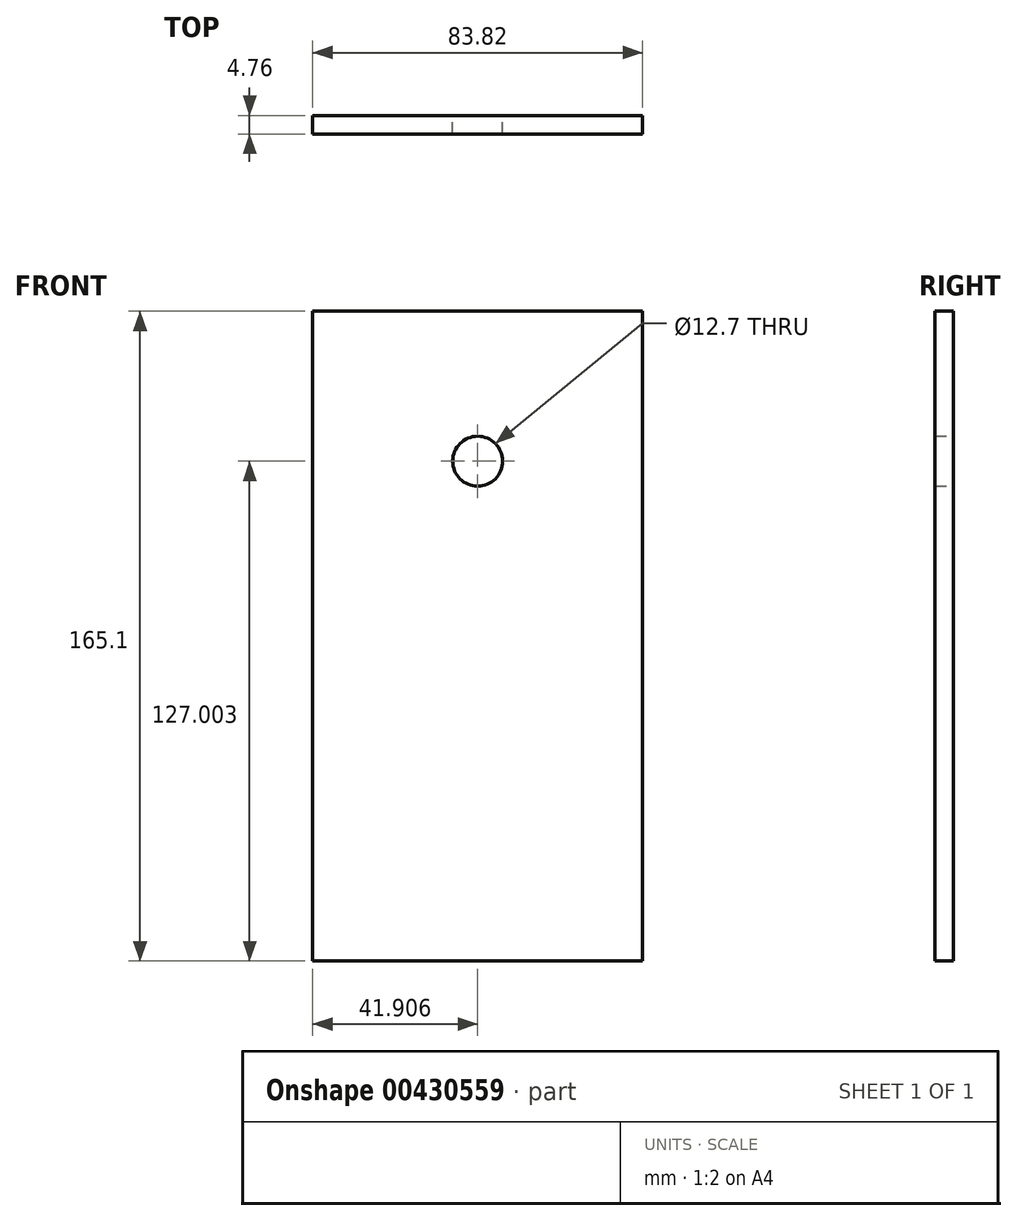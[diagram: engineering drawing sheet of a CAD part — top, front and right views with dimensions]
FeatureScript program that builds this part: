
annotation { "Feature Type Name" : "Feature", "Feature Type Description" : "" }
export const myFeature = defineFeature(function(context is Context, id is Id, definition is map)
    precondition{}
    {
        {
            var Q0;
            Q0=qCreatedBy(makeId("Front.planeOp"),FACE);
            var sketch = newSketch(context, id + "F0", { "sketchPlane" : qUnion([Q0])});
            skLineSegment(sketch, "E0.bottom", {"start": v(-47.77, 108.25) * mm, "end": v(36.05, 108.25) * mm});
            skLineSegment(sketch, "E0.top", {"start": v(-47.77, -56.85) * mm, "end": v(36.05, -56.85) * mm});
            skLineSegment(sketch, "E0.left", {"start": v(-47.77, 108.25) * mm, "end": v(-47.77, -56.85) * mm});
            skLineSegment(sketch, "E0.right", {"start": v(36.05, 108.25) * mm, "end": v(36.05, -56.85) * mm});
            skPoint(sketch, "E1", {"position": v(-5.86, 108.25) * mm});
            skPoint(sketch, "E2", {"position": v(-5.86, 70.15) * mm});
            skCircle(sketch, "E3", {"center": v(-5.86, 70.15) * mm, "radius": 6.35 * mm});
            skSolve(sketch);
        }
        {
            var Q0;
            Q0=makeQuery(id+"F0.imprint","IMPRINT",FACE,{"disambiguationData":[TD([[makeQuery(id+"F0.imprint","IMPRINT",EDGE,{"derivedFrom":sQuery(id+"F0.wireOp",EDGE,"E0.bottom")}),-1.0]])]});
            extrude(context, id + "F1", {"entities" : qUnion([Q0]), "depth" : 4.76 * mm});
        }
    });
